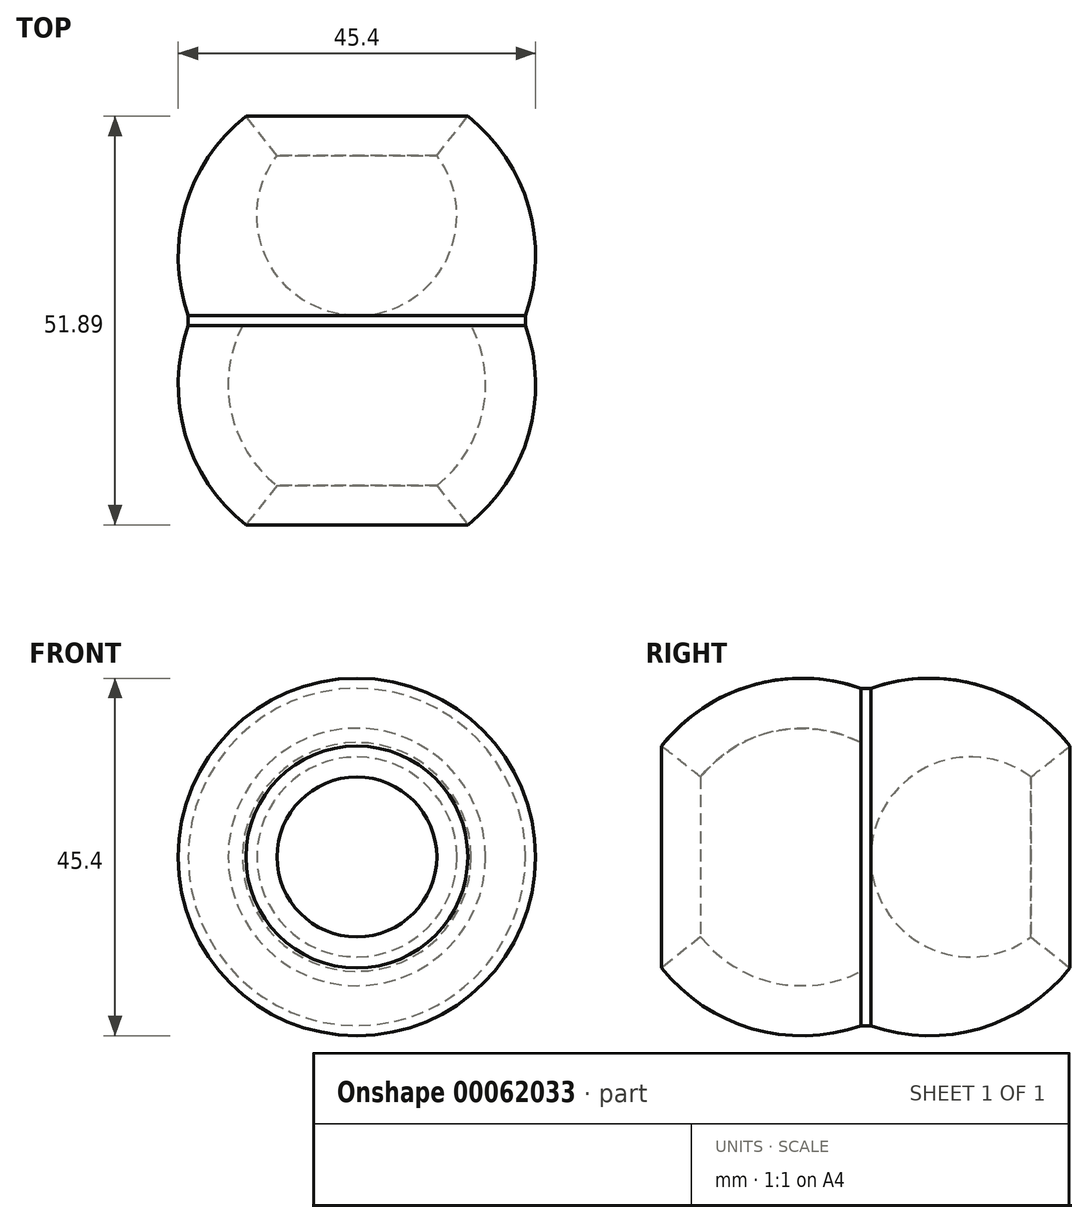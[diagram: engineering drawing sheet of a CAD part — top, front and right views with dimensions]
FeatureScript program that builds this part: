
annotation { "Feature Type Name" : "Feature", "Feature Type Description" : "" }
export const myFeature = defineFeature(function(context is Context, id is Id, definition is map)
    precondition{}
    {
        {
            var Q0;
            Q0=qCreatedBy(makeId("Top.planeOp"),FACE);
            var sketch = newSketch(context, id + "F0", { "sketchPlane" : qUnion([Q0])});
            skArc(sketch, "E0", {"start": v(-6.35, 10.19) * mm, "mid": v(0, -13.51) * mm, "end": v(6.35, 10.19) * mm});
            skLineSegment(sketch, "E1", {"start": v(-6.35, 10.19) * mm, "end": v(6.35, 10.19) * mm});
            skPoint(sketch, "E2.orphan", {"position": v(0, 28.68) * mm});
            skArc(sketch, "E3", {"start": v(-10.15, 6.82) * mm, "mid": v(-15.99, -2.56) * mm, "end": v(-14.53, -13.51) * mm});
            skArc(sketch, "E4.0", {"start": v(-14.1, 11.8) * mm, "mid": v(-21.8, 0.32) * mm, "end": v(-21.43, -13.51) * mm});
            skLineSegment(sketch, "E5", {"start": v(-14.1, 11.8) * mm, "end": v(-10.15, 6.82) * mm});
            skLineSegment(sketch, "E6", {"start": v(14.1, 11.8) * mm, "end": v(10.15, 6.82) * mm});
            skLineSegment(sketch, "E7", {"start": v(0, 10.19) * mm, "end": v(0, -13.51) * mm});
            skArc(sketch, "E8.trimOffspring", {"start": v(14.53, -13.51) * mm, "mid": v(15.99, -2.56) * mm, "end": v(10.15, 6.82) * mm});
            skArc(sketch, "E9.trimOffspring", {"start": v(21.43, -13.51) * mm, "mid": v(21.8, 0.32) * mm, "end": v(14.1, 11.8) * mm});
            skLineSegment(sketch, "E10", {"start": v(-31.92, -13.51) * mm, "end": v(30.77, -13.51) * mm});
            skLineSegment(sketch, "E11.bottom", {"start": v(-21.43, -13.51) * mm, "end": v(21.43, -13.51) * mm});
            skLineSegment(sketch, "E11.top", {"start": v(-21.43, -14.78) * mm, "end": v(21.43, -14.78) * mm});
            skLineSegment(sketch, "E11.left", {"start": v(-21.43, -13.51) * mm, "end": v(-21.43, -14.78) * mm});
            skLineSegment(sketch, "E11.right", {"start": v(21.43, -13.51) * mm, "end": v(21.43, -14.78) * mm});
            skLineSegment(sketch, "E12", {"start": v(21.43, -14.15) * mm, "end": v(-21.43, -14.15) * mm, "construction": true});
            skArc(sketch, "E13.MirrorCS", {"start": v(-14.1, -40.09) * mm, "mid": v(-21.8, -28.6) * mm, "end": v(-21.43, -14.78) * mm});
            skArc(sketch, "E14.MirrorCS", {"start": v(-10.15, -35.11) * mm, "mid": v(-15.99, -25.73) * mm, "end": v(-14.53, -14.78) * mm});
            skArc(sketch, "E15.MirrorCS", {"start": v(-6.35, -38.48) * mm, "mid": v(0, -14.78) * mm, "end": v(6.35, -38.48) * mm});
            skLineSegment(sketch, "E16.MirrorCS", {"start": v(-6.35, -38.48) * mm, "end": v(6.35, -38.48) * mm});
            skLineSegment(sketch, "E17.MirrorCS", {"start": v(-14.1, -40.09) * mm, "end": v(-10.15, -35.11) * mm});
            skLineSegment(sketch, "E18.MirrorCS", {"start": v(14.1, -40.09) * mm, "end": v(10.15, -35.11) * mm});
            skLineSegment(sketch, "E19.MirrorCS", {"start": v(0, -38.48) * mm, "end": v(0, -14.78) * mm});
            skArc(sketch, "E20.MirrorCS", {"start": v(21.43, -14.78) * mm, "mid": v(21.8, -28.6) * mm, "end": v(14.1, -40.09) * mm});
            skArc(sketch, "E21.MirrorCS", {"start": v(14.53, -14.78) * mm, "mid": v(15.99, -25.73) * mm, "end": v(10.15, -35.11) * mm});
            skLineSegment(sketch, "E22", {"start": v(0, -13.51) * mm, "end": v(0, -14.78) * mm});
            skSolve(sketch);
        }
        {
            var Q0;
            {var subQ0=sQuery(id+"F0.wireOp",EDGE,"E3");Q0=makeQuery(id+"F0.imprint","IMPRINT",FACE,{"disambiguationData":[TD([[makeQuery(id+"F0.imprint","IMPRINT",EDGE,{"derivedFrom":subQ0}),1.0]])]});}
            var Q1;
            {var subQ0=sQuery(id+"F0.wireOp",EDGE,"E3");Q1=makeQuery(id+"F0.imprint","IMPRINT",FACE,{"disambiguationData":[TD([[makeQuery(id+"F0.imprint","IMPRINT",EDGE,{"derivedFrom":subQ0}),-1.0]])]});}
            var Q2;
            {var subQ5=sQuery(id+"F0.wireOp",EDGE,"E11.left");Q2=makeQuery(id+"F0.imprint","IMPRINT",FACE,{"disambiguationData":[TD([[makeQuery(id+"F0.imprint","IMPRINT",EDGE,{"derivedFrom":subQ5}),1.0]])]});}
            var Q3;
            {var subQ0=sQuery(id+"F0.wireOp",EDGE,"E14.MirrorCS");Q3=makeQuery(id+"F0.imprint","IMPRINT",FACE,{"disambiguationData":[TD([[makeQuery(id+"F0.imprint","IMPRINT",EDGE,{"derivedFrom":subQ0}),-1.0]])]});}
            var Q4;
            {var subQ0=sQuery(id+"F0.wireOp",EDGE,"E13.MirrorCS");Q4=makeQuery(id+"F0.imprint","IMPRINT",FACE,{"disambiguationData":[TD([[makeQuery(id+"F0.imprint","IMPRINT",EDGE,{"derivedFrom":subQ0}),-1.0]])]});}
            var Q5;
            Q5=sQuery(id+"F0.wireOp",EDGE,"E22");
            revolve(context, id + "F1", {"entities" : qUnion([Q0, Q1, Q2, Q3, Q4]), "axis" : qUnion([Q5]), "revolveType" : RevolveType.FULL});
        }
    });
